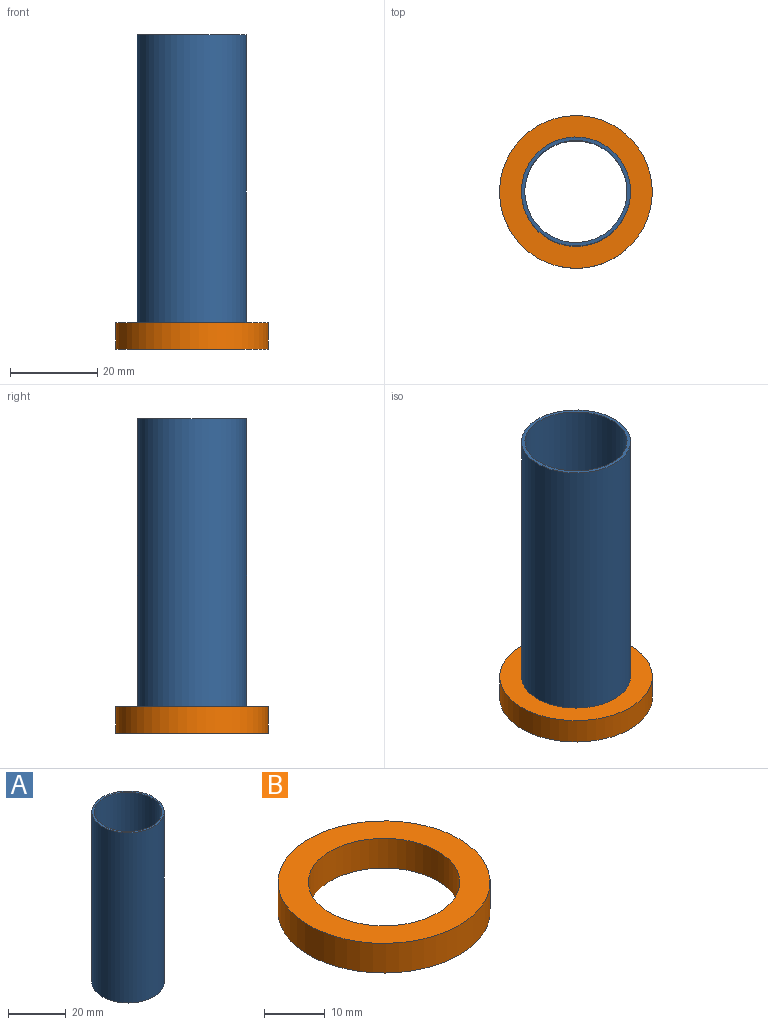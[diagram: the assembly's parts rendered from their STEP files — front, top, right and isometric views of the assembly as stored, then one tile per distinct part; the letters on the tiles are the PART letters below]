
ASSEMBLY  parts=2 mates=1
PART A: 4 faces, bbox 25x25x72 mm
  f0: cylinder r=11.7mm len=72mm, axis (0,0,-1), area 5293mm2, adj f2,f3
  f1: cylinder r=12.5mm len=72mm, axis (0,0,-1), area 5654.9mm2, adj f2,f3
  f2: plane 25x25mm, normal (0,0,1), area 60.8mm2, adj f0,f1
  f3: plane 25x25mm, normal (0,0,-1), area 60.8mm2, adj f0,f1
PART B: 4 faces, bbox 35x35x6 mm
  f0: cylinder r=12.5mm len=25mm, axis (0,0,-1), area 471.2mm2, adj f2,f3
  f1: cylinder r=17.5mm len=35mm, axis (0,0,-1), area 659.7mm2, adj f2,f3
  f2: plane 35x35mm, normal (0,0,1), area 471.2mm2, adj f0,f1
  f3: plane 35x35mm, normal (0,0,-1), area 471.2mm2, adj f0,f1
PLACE A at identity
PLACE B at identity fixed
MATE fastened A.f0 <-> B.f0  axis (0,0,-1) through (0,0,0)mm
